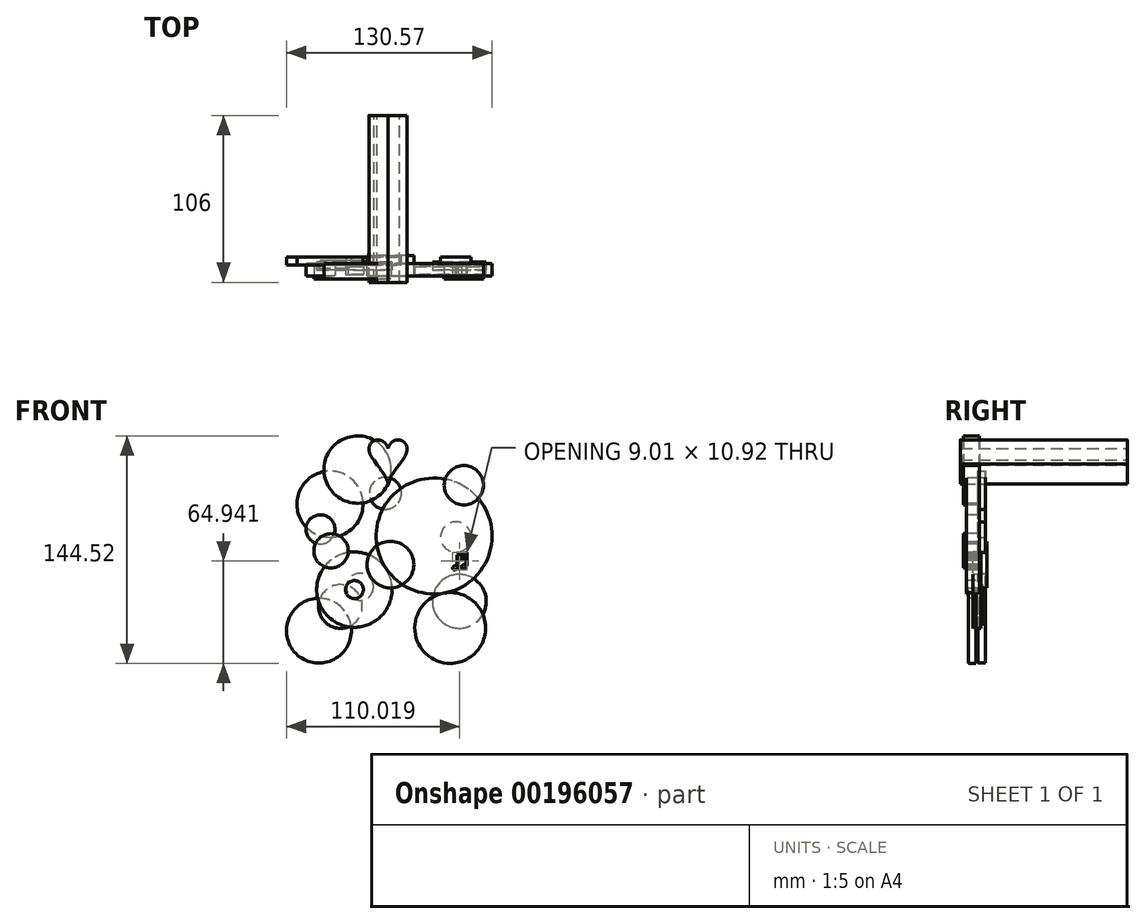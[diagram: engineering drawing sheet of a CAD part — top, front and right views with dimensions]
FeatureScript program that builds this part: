
annotation { "Feature Type Name" : "Feature", "Feature Type Description" : "" }
export const myFeature = defineFeature(function(context is Context, id is Id, definition is map)
    precondition{}
    {
        {
            var Q0;
            Q0=qCreatedBy(makeId("Front.planeOp"),FACE);
            var sketch = newSketch(context, id + "F0", { "sketchPlane" : qUnion([Q0])});
            skLineSegment(sketch, "E0.bottom", {"start": v(-100.95, 104.06) * mm, "end": v(102.05, 104.06) * mm});
            skLineSegment(sketch, "E0.top", {"start": v(-100.95, -98.94) * mm, "end": v(102.05, -98.94) * mm});
            skLineSegment(sketch, "E0.left", {"start": v(-100.95, 104.06) * mm, "end": v(-100.95, -98.94) * mm});
            skLineSegment(sketch, "E0.right", {"start": v(102.05, 104.06) * mm, "end": v(102.05, -98.94) * mm});
            skSolve(sketch);
        }
        {
            var Q0;
            Q0=makeQuery(id+"F0.imprint","IMPRINT",FACE,{"disambiguationData":[TD([[makeQuery(id+"F0.imprint","IMPRINT",EDGE,{"derivedFrom":sQuery(id+"F0.wireOp",EDGE,"E0.bottom")}),-1.0]])]});
            var sketch = newSketch(context, id + "F1", { "sketchPlane" : qUnion([Q0])});
            skCircle(sketch, "E1", {"center": v(-50.54, -74.33) * mm, "radius": 20.58 * mm});
            skSolve(sketch);
        }
        {
            var Q0;
            Q0 = qSketchRegion(id + "F1", true);
            extrude(context, id + "F2", {"entities" : qUnion([Q0]), "depth" : 5 * mm});
        }
        {
            var Q0;
            Q0=makeQuery(id+"F2.opExtrude","CAP_FACE",FACE,{"disambiguationData":[OSD([sQuery(id+"F1.wireOp",EDGE,"E1")])],"isStart":false});
            var sketch = newSketch(context, id + "F3", { "sketchPlane" : qUnion([Q0])});
            skCircle(sketch, "E2", {"center": v(-36.87, -58.94) * mm, "radius": 13.88 * mm});
            skSolve(sketch);
        }
        {
            var Q0;
            Q0 = qSketchRegion(id + "F3", true);
            extrude(context, id + "F4", {"entities" : qUnion([Q0]), "operationType" : NewBodyOperationType.ADD, "oppositeDirection" : true, "depth" : 3 * mm, "hasSecondDirection" : true, "secondDirectionOppositeDirection" : false, "secondDirectionDepth" : 2 * mm});
        }
        {
            var Q0;
            Q0=makeQuery(id+"F4.opExtrude","CAP_FACE",FACE,{"disambiguationData":[OSD([sQuery(id+"F3.wireOp",EDGE,"E2")])],"isStart":true});
            var sketch = newSketch(context, id + "F5", { "sketchPlane" : qUnion([Q0])});
            skCircle(sketch, "E3", {"center": v(-28.03, -48.25) * mm, "radius": 23.93 * mm});
            skCircle(sketch, "E4", {"center": v(38.57, -55.68) * mm, "radius": 17.11 * mm});
            skSolve(sketch);
        }
        {
            var Q0;
            Q0 = qSketchRegion(id + "F5", true);
            extrude(context, id + "F6", {"entities" : qUnion([Q0]), "operationType" : NewBodyOperationType.ADD, "oppositeDirection" : true, "depth" : 4 * mm, "hasSecondDirection" : true, "secondDirectionOppositeDirection" : false, "secondDirectionDepth" : 1 * mm});
        }
        {
            var Q0;
            Q0=makeQuery(id+"F6.opExtrude","CAP_FACE",FACE,{"disambiguationData":[OSD([sQuery(id+"F5.wireOp",EDGE,"E3")])],"isStart":true});
            var sketch = newSketch(context, id + "F7", { "sketchPlane" : qUnion([Q0])});
            skCircle(sketch, "E5", {"center": v(32.82, -72.62) * mm, "radius": 22.5 * mm});
            skCircle(sketch, "E6", {"center": v(-28.03, -48.25) * mm, "radius": 5.7 * mm});
            skSolve(sketch);
        }
        {
            var Q0;
            Q0 = qSketchRegion(id + "F7", true);
            extrude(context, id + "F8", {"entities" : qUnion([Q0]), "oppositeDirection" : true, "depth" : 2 * mm, "hasSecondDirection" : true, "secondDirectionOppositeDirection" : false, "secondDirectionDepth" : 3 * mm});
        }
        {
            var Q0;
            Q0=makeQuery(id+"F8.opExtrude","CAP_FACE",FACE,{"disambiguationData":[OSD([sQuery(id+"F7.wireOp",EDGE,"E5")])],"isStart":true});
            var sketch = newSketch(context, id + "F9", { "sketchPlane" : qUnion([Q0])});
            skCircle(sketch, "E7", {"center": v(22.63, -14.19) * mm, "radius": 36.82 * mm});
            skCircle(sketch, "E8", {"center": v(-49.57, -9.97) * mm, "radius": 9.23 * mm});
            skSolve(sketch);
        }
        {
            var Q0;
            Q0 = qSketchRegion(id + "F9", true);
            extrude(context, id + "F10", {"entities" : qUnion([Q0]), "oppositeDirection" : true, "depth" : 7 * mm, "hasSecondDirection" : true, "secondDirectionOppositeDirection" : false, "secondDirectionDepth" : 1 * mm});
        }
        {
            var Q0;
            Q0=makeQuery(id+"F10.opExtrude","CAP_FACE",FACE,{"disambiguationData":[OSD([sQuery(id+"F9.wireOp",EDGE,"E8")])],"isStart":true});
            var sketch = newSketch(context, id + "F11", { "sketchPlane" : qUnion([Q0])});
            skCircle(sketch, "E9", {"center": v(-42.87, -23.62) * mm, "radius": 10.9 * mm});
            skCircle(sketch, "E10", {"center": v(-26, 28) * mm, "radius": 21.42 * mm});
            skCircle(sketch, "E11", {"center": v(41.5, 18.07) * mm, "radius": 12.47 * mm});
            skSolve(sketch);
        }
        {
            var Q0;
            Q0 = qSketchRegion(id + "F11", true);
            extrude(context, id + "F12", {"entities" : qUnion([Q0]), "oppositeDirection" : true, "depth" : 8 * mm, "hasSecondDirection" : true, "secondDirectionOppositeDirection" : false, "secondDirectionDepth" : 2 * mm});
        }
        {
            var Q0;
            Q0=makeQuery(id+"F0.imprint","IMPRINT",FACE,{"disambiguationData":[TD([[makeQuery(id+"F0.imprint","IMPRINT",EDGE,{"derivedFrom":sQuery(id+"F0.wireOp",EDGE,"E0.bottom")}),-1.0]])]});
            var sketch = newSketch(context, id + "F13", { "sketchPlane" : qUnion([Q0])});
            skCircle(sketch, "E12", {"center": v(-8.34, 12.94) * mm, "radius": 10.18 * mm});
            skCircle(sketch, "E13", {"center": v(-43.53, 6.05) * mm, "radius": 21.02 * mm});
            skCircle(sketch, "E14", {"center": v(36.41, -14.81) * mm, "radius": 9.67 * mm});
            skCircle(sketch, "E15", {"center": v(-24.5, -46.45) * mm, "radius": 8.56 * mm});
            skSolve(sketch);
        }
        {
            var Q0;
            Q0 = qSketchRegion(id + "F13", true);
            extrude(context, id + "F14", {"entities" : qUnion([Q0]), "depth" : 5 * mm});
        }
        {
            var Q0;
            Q0=makeQuery(id+"F0.imprint","IMPRINT",FACE,{"disambiguationData":[TD([[makeQuery(id+"F0.imprint","IMPRINT",EDGE,{"derivedFrom":sQuery(id+"F0.wireOp",EDGE,"E0.bottom")}),-1.0]])]});
            var sketch = newSketch(context, id + "F15", { "sketchPlane" : qUnion([Q0])});
            skCircle(sketch, "E16", {"center": v(-5.13, -32.36) * mm, "radius": 14.83 * mm});
            skSolve(sketch);
        }
        {
            var Q0;
            Q0 = qSketchRegion(id + "F15", true);
            extrude(context, id + "F16", {"entities" : qUnion([Q0]), "depth" : 12 * mm, "hasSecondDirection" : true, "secondDirectionOppositeDirection" : true, "secondDirectionDepth" : 1 * mm});
        }
        {
            var Q0;
            Q0=makeQuery(id+"F0.imprint","IMPRINT",FACE,{"disambiguationData":[TD([[makeQuery(id+"F0.imprint","IMPRINT",EDGE,{"derivedFrom":sQuery(id+"F0.wireOp",EDGE,"E0.bottom")}),-1.0]])]});
            var sketch = newSketch(context, id + "F17", { "sketchPlane" : qUnion([Q0])});
            skText(sketch, "E17", { "text": "♥", "fontName": "Arimo-Regular.ttf"});
            skLineSegment(sketch, "E18", {"start": v(-50.55, -94.94) * mm, "end": v(33.32, -94.94) * mm});
            const initialGuessF17  = {"E17": [-0.0212, 0.01954, 1, 0, 0.03522]};
            skSetInitialGuess(sketch, initialGuessF17);
            skSolve(sketch);
        }
        {
            var Q0;
            Q0 = qSketchRegion(id + "F17", true);
            extrude(context, id + "F18", {"entities" : qUnion([Q0]), "depth" : 16 * mm, "hasSecondDirection" : true, "secondDirectionOppositeDirection" : true, "secondDirectionDepth" : 90 * mm});
        }
        {
            var Q0;
            Q0=makeQuery(id+"F10.opExtrude","CAP_FACE",FACE,{"disambiguationData":[OSD([sQuery(id+"F9.wireOp",EDGE,"E7")])],"isStart":true});
            var sketch = newSketch(context, id + "F19", { "sketchPlane" : qUnion([Q0])});
            skText(sketch, "E19", { "text": "♫", "fontName": "NotoSerif-Regular.ttf"});
            const initialGuessF19  = {"E19": [0.03192, -0.03524, 1, 0, 0.0134]};
            skSetInitialGuess(sketch, initialGuessF19);
            skSolve(sketch);
        }
        {
            var Q0;
            Q0 = qSketchRegion(id + "F19", true);
            extrude(context, id + "F20", {"entities" : qUnion([Q0]), "operationType" : NewBodyOperationType.REMOVE, "oppositeDirection" : true, "depth" : 25 * mm});
        }
    });
